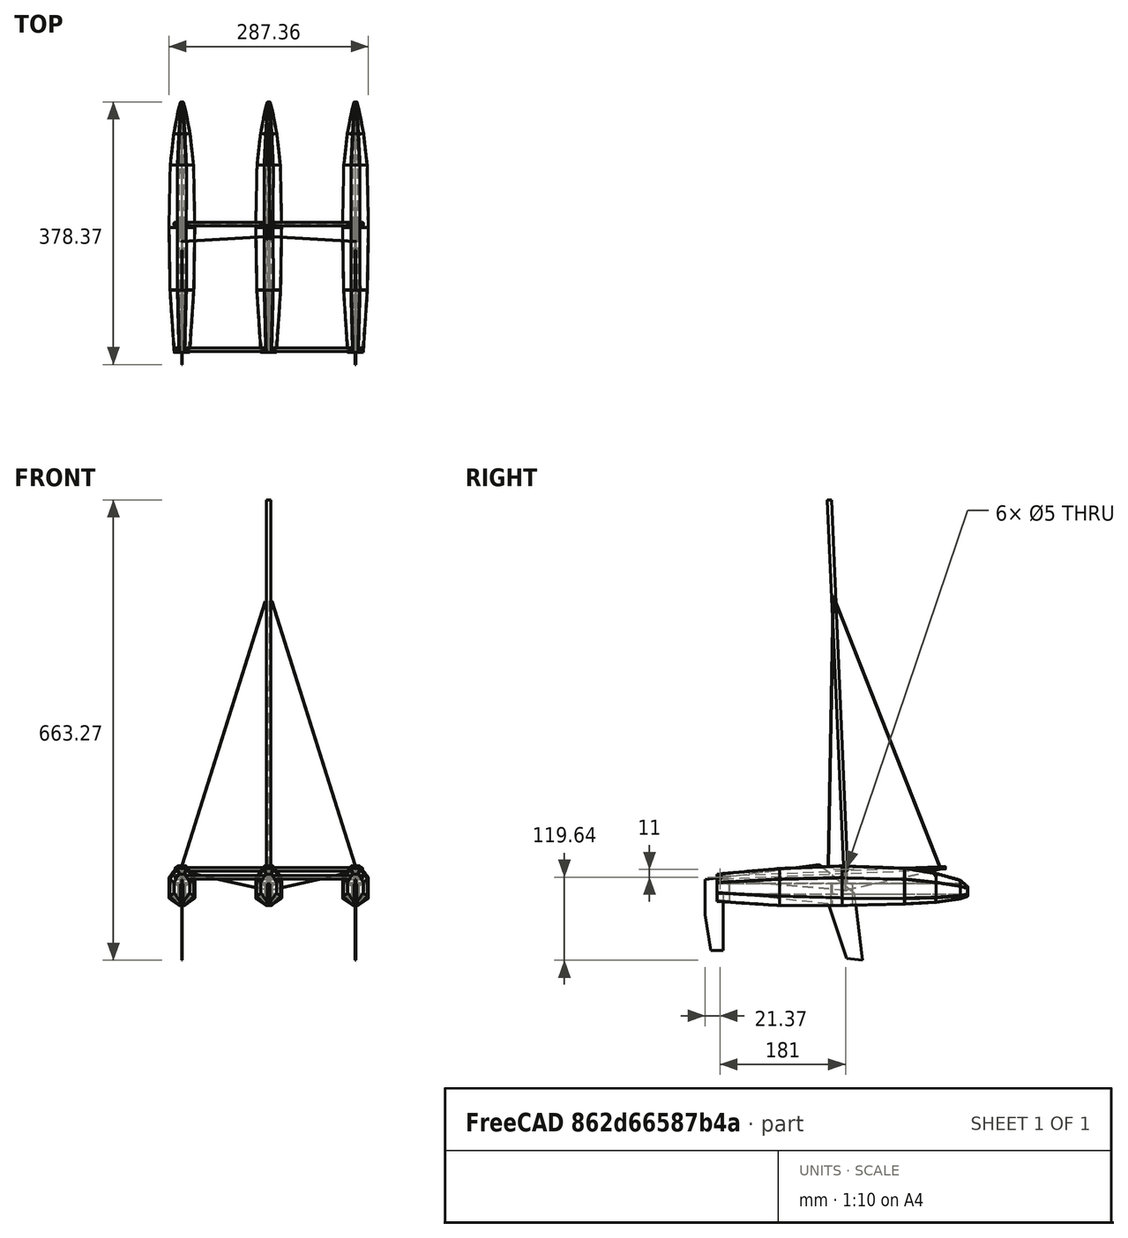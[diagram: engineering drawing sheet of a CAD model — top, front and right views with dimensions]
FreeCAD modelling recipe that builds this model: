
FCSTD DOCUMENT  (FreeCAD 0.18R4 (GitTag))
Label: O-Cat Assembly
License: All rights reserved
LicenseURL: http://en.wikipedia.org/wiki/All_rights_reserved
objects: Part::Feature×13, Part::Cylinder×12, Part::Cut×2, Part::MultiFuse×1, Sketcher::SketchObject×1
note: 29 computed .brp shape members not serialized (recipe doc carries the construction recipe); baked Part::Feature solids carry a one-line shape summary decoded from their .brp

FEATURE [Part::Feature] Part__Feature  label="Back_Post"
  shape: bbox 32.4 x 90 x 51.62 mm, 13 faces (baked)
FEATURE [Part::Feature] Part__Feature001  label="Centerboard_Cuts"
  shape: bbox 97.62 x 449.3 x 72 mm, 16 faces (baked)
FEATURE [Part::Feature] Part__Feature002  label="Centerboard"
  shape: bbox 7 x 180 x 31 mm, 7 faces (baked)
FEATURE [Part::Feature] Part__Feature003  label="Front_Post"
  shape: bbox 35.36 x 180 x 55.22 mm, 25 faces (baked)
FEATURE [Part::Feature] Part__Feature004  label="Infill_Ribs"
  shape: bbox 35.36 x 360 x 55.22 mm, 58 faces (baked)
FEATURE [Part::Feature] Part__Feature005  label="Nose_Post"
  shape: bbox 31.69 x 80 x 25.2 mm, 9 faces (baked)
FEATURE [Part::Feature] Part__Feature006  label="Post_Cut"
  shape: bbox 210 x 436.5 x 131 mm, 12 faces (baked)
FEATURE [Part::Feature] Part__Feature007  label="Rudder"
  shape: bbox 32.4 x 90 x 31 mm, 8 faces (baked)
FEATURE [Part::Feature] Part__Feature008  label="Skin"
  shape: bbox 40.5 x 374.2 x 61.4 mm, 243 faces (baked)
FEATURE [Part::MultiFuse] Fusion
  Refine = true
  Shapes = -> [Part__Feature008,Part__Feature007,Part__Feature005,Part__Feature004,Part__Feature003,Part__Feature002,Part__Feature]
FEATURE [Part::Cut] Cut
  Base = -> Fusion
  Tool = -> Part__Feature006
FEATURE [Part::Cut] Cut001
  Base = -> Cut
  Tool = -> Part__Feature001
FEATURE [Part::Feature] Part__Feature009  label="Cut002"
  Placement = pos=(125,0,0) rot=(0,0,1;0rad)
  shape: bbox 40.5 x 374.2 x 61.4 mm, 387 faces (baked)
FEATURE [Part::Feature] Part__Feature010  label="Cut003"
  Placement = pos=(-125,0,0) rot=(0,0,1;0rad)
  shape: bbox 40.5 x 374.2 x 61.4 mm, 387 faces (baked)
FEATURE [Part::Cylinder] Cylinder
  Angle = 360
  AttacherType = Attacher::AttachEngine3D
  Height = 270
  Placement = pos=(-135,5,-17) rot=(0,1,0;1.5708rad)
  Radius = 2.5
FEATURE [Part::Cylinder] Cylinder001
  Angle = 360
  AttacherType = Attacher::AttachEngine3D
  Height = 270
  Placement = pos=(-135,-176,-28) rot=(0,1,0;1.5708rad)
  Radius = 2.5
FEATURE [Part::Cylinder] Cylinder002
  Angle = 360
  AttacherType = Attacher::AttachEngine3D
  Height = 530
  Placement = pos=(0,5,-14) rot=(1,0,0;0.043633rad)
  Radius = 3
FEATURE [Sketcher::SketchObject] Sketch
  Placement = pos=(0,0,0) rot=(0.57735,0.57735,0.57735;2.0944rad)
  sketch-geometry (12):
    g0: LineSegment StartX=-19.6916 StartY=516.423 StartZ=0 EndX=-54.926 EndY=522.174 EndZ=0
    g1: LineSegment StartX=-54.926 StartY=522.174 StartZ=0 EndX=-94.7913 EndY=369.56 EndZ=0
    g2: LineSegment StartX=-94.7913 StartY=369.56 StartZ=0 EndX=-127.917 EndY=159.114 EndZ=0
    g3: LineSegment StartX=-127.917 StartY=159.114 StartZ=0 EndX=-148.903 EndY=-5.46047 EndZ=0
    g4: LineSegment StartX=-148.903 StartY=-5.46047 StartZ=0 EndX=3.79079 EndY=-5.46047 EndZ=0
    g5: LineSegment StartX=3.79079 StartY=-5.46047 StartZ=0 EndX=-19.6916 EndY=516.423 EndZ=0
    g6: LineSegment StartX=-5.17071 StartY=343.5 StartZ=0 EndX=121.738 EndY=-12.5431 EndZ=0
    g7: LineSegment StartX=12.9713 StartY=15.4788 StartZ=0 EndX=4.89644 EndY=206.715 EndZ=0
    g8: LineSegment StartX=13.1017 StartY=242.822 StartZ=0 EndX=28.443 EndY=249.197 EndZ=0
    g9: LineSegment StartX=13.1017 StartY=242.822 StartZ=0 EndX=4.89644 EndY=206.715 EndZ=0
    g10: LineSegment StartX=12.9713 StartY=15.4788 StartZ=0 EndX=71.2661 EndY=-8.68279 EndZ=0
    g11: LineSegment StartX=71.2661 StartY=-8.68279 StartZ=0 EndX=121.738 EndY=-12.5431 EndZ=0
  constraints (13):
    c: Coincident(g1,g2)
    c: Coincident(g2,g3)
    c: Coincident(g3,g4)
    c: Coincident(g4,g5)
    c: Coincident(g5,g0)
    c: Coincident(g1,g0)
    c: Horizontal(g4)
    c: PointOnObject(g8,g6)
    c: Coincident(g9,g8)
    c: Coincident(g9,g7)
    c: Coincident(g10,g7)
    c: Coincident(g11,g10)
    c: Coincident(g11,g6)
FEATURE [Part::Cylinder] Cylinder003
  Angle = 360
  AttacherType = Attacher::AttachEngine3D
  Height = 320
  Placement = pos=(0,-171.01,-28.3053) rot=(-1,0,0;1.52716rad)
  Radius = 2
FEATURE [Part::Cylinder] Cylinder004
  Angle = 360
  AttacherType = Attacher::AttachEngine3D
  Height = 25
  Placement = pos=(3e-15,5,-22) rot=(0,1,0;3.14159rad)
  Radius = 2
FEATURE [Part::Cylinder] Cylinder005
  Angle = 360
  AttacherType = Attacher::AttachEngine3D
  Height = 175
  Placement = pos=(0,-171.271,-31.2939) rot=(-1,0,0;1.65806rad)
  Radius = 0.25
FEATURE [Part::Cylinder] Cylinder006
  Angle = 360
  AttacherType = Attacher::AttachEngine3D
  Height = 140
  Placement = pos=(0.215783,5.36884,-46.4364) rot=(0.004281,0.626014,0.7798;3.1491rad)
  Radius = 0.25
FEATURE [Part::Cylinder] Cylinder007
  Angle = 360
  AttacherType = Attacher::AttachEngine3D
  Height = 120
  Placement = pos=(0,5,-47) rot=(0,1,0;1.35263rad)
  Radius = 0.25
FEATURE [Part::Cylinder] Cylinder008
  Angle = 360
  AttacherType = Attacher::AttachEngine3D
  Height = 120
  Placement = pos=(0,5,-47) rot=(0,-1,0;1.35263rad)
  Radius = 0.25
FEATURE [Part::Cylinder] Cylinder009
  Angle = 360
  AttacherType = Attacher::AttachEngine3D
  Height = 400
  Placement = pos=(125,-20,-12) rot=(-0.056606,-0.998359,-0.008713;0.305927rad)
  Radius = 0.25
FEATURE [Part::Cylinder] Cylinder010
  Angle = 360
  AttacherType = Attacher::AttachEngine3D
  Height = 400
  Placement = pos=(-125,-20,-12) rot=(-0.056606,0.998359,0.008713;0.305927rad)
  Radius = 0.25
FEATURE [Part::Cylinder] Cylinder011
  Angle = 360
  AttacherType = Attacher::AttachEngine3D
  Height = 420
  Placement = pos=(0.527071,140.75,-13.1803) rot=(0.001348,-0.186395,0.982474;3.13833rad)
  Radius = 0.25
FEATURE [Part::Feature] Part__Feature013  label="Body001"
  Placement = pos=(125,0,-10) rot=(1,0,0;0rad)
  shape: bbox 1 x 226.7 x 137.6 mm, 12 faces (baked)
FEATURE [Part::Feature] Part__Feature014  label="Body002"
  Placement = pos=(-125,0,-10) rot=(1,0,0;0rad)
  shape: bbox 1 x 226.7 x 137.6 mm, 12 faces (baked)
